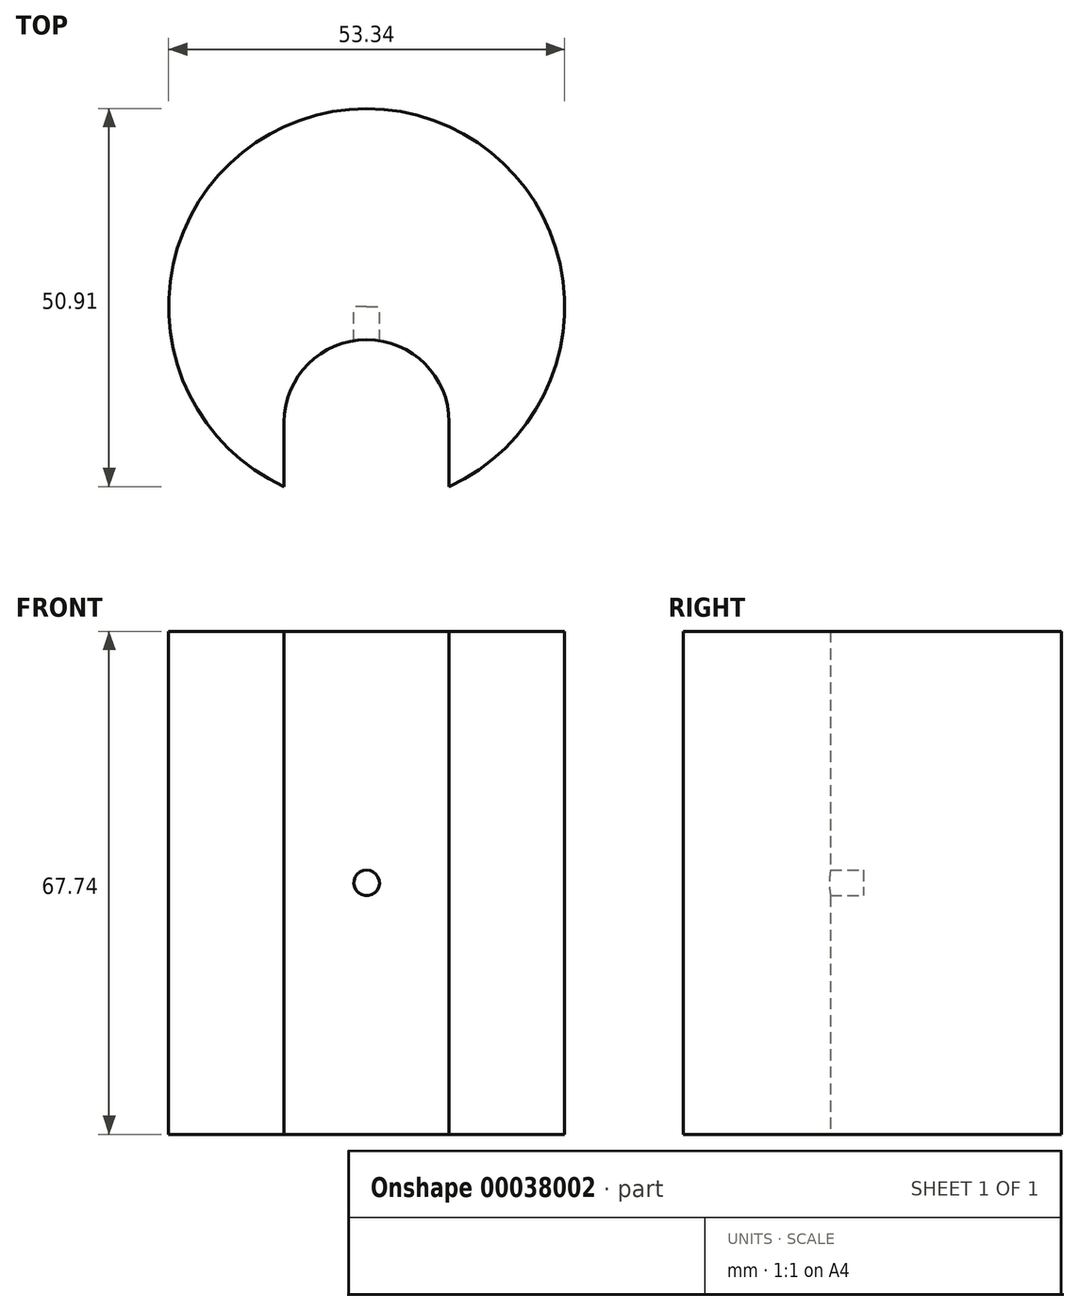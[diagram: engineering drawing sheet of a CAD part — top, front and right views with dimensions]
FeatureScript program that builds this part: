
annotation { "Feature Type Name" : "Feature", "Feature Type Description" : "" }
export const myFeature = defineFeature(function(context is Context, id is Id, definition is map)
    precondition{}
    {
        {
            var Q0;
            Q0=qCreatedBy(makeId("Top.planeOp"),FACE);
            var sketch = newSketch(context, id + "F0", { "sketchPlane" : qUnion([Q0])});
            skCircle(sketch, "E0", {"center": v(0, 0) * mm, "radius": 26.67 * mm});
            skSolve(sketch);
        }
        {
            var Q0;
            Q0 = qSketchRegion(id + "F0", true);
            extrude(context, id + "F1", {"entities" : qUnion([Q0]), "depth" : 67.74 * mm});
        }
        {
            var Q0;
            Q0=makeQuery(id+"F1.opExtrude","CAP_FACE",FACE,{"disambiguationData":[OSD([sQuery(id+"F0.wireOp",EDGE,"E0")])],"isStart":false});
            var sketch = newSketch(context, id + "F2", { "sketchPlane" : qUnion([Q0])});
            skLineSegment(sketch, "E1", {"start": v(0, 0) * mm, "end": v(0, -15.56) * mm, "construction": true});
            skLineSegment(sketch, "E2.rect.bottom", {"start": v(11.11, -26.67) * mm, "end": v(-11.11, -26.67) * mm});
            skLineSegment(sketch, "E2.rect.top", {"start": v(11.11, -4.45) * mm, "end": v(-11.11, -4.45) * mm});
            skLineSegment(sketch, "E2.rect.left", {"start": v(11.11, -26.67) * mm, "end": v(11.11, -4.45) * mm});
            skLineSegment(sketch, "E2.rect.right", {"start": v(-11.11, -26.67) * mm, "end": v(-11.11, -4.45) * mm});
            skPoint(sketch, "E2.rect.middle", {"position": v(0, -15.56) * mm});
            skSolve(sketch);
        }
        {
            var Q0;
            Q0 = qSketchRegion(id + "F2", true);
            var Q1;
            Q1=makeQuery(id+"F1.opExtrude","CAP_FACE",FACE,{"disambiguationData":[OSD([sQuery(id+"F0.wireOp",EDGE,"E0")])],"isStart":true});
            extrude(context, id + "F3", {"entities" : qUnion([Q0]), "operationType" : NewBodyOperationType.REMOVE, "endBound" : BoundingType.UP_TO_SURFACE, "oppositeDirection" : true, "endBoundEntityFace" : qUnion([Q1]), "depth" : 25.4 * mm});
        }
        {
            var Q0;
            Q0=makeQuery(id+"F3.boolean.opBoolean","COPY",EDGE,{"derivedFrom":makeQuery(id+"F3.opExtrude","SWEPT_EDGE",EDGE,{"disambiguationData":[OSD([sQuery(id+"F2.wireOp",EDGE,"E2.rect.top"),sQuery(id+"F2.wireOp",EDGE,"E2.rect.left")])]})});
            var Q1;
            Q1=makeQuery(id+"F3.boolean.opBoolean","COPY",EDGE,{"derivedFrom":makeQuery(id+"F3.opExtrude","SWEPT_EDGE",EDGE,{"disambiguationData":[OSD([sQuery(id+"F2.wireOp",EDGE,"E2.rect.top"),sQuery(id+"F2.wireOp",EDGE,"E2.rect.right")])]})});
            fillet(context, id + "F4", {"entities" : qUnion([Q0, Q1]), "radius" : 11.1 * mm, "tangentPropagation" : true, "allowEdgeOverflow" : false});
        }
        {
            var Q0;
            Q0=qCreatedBy(makeId("Front.planeOp"),FACE);
            var sketch = newSketch(context, id + "F5", { "sketchPlane" : qUnion([Q0])});
            skCircle(sketch, "E3", {"center": v(0, 33.87) * mm, "radius": 1.73 * mm});
            skLineSegment(sketch, "E4", {"start": v(0, 67.74) * mm, "end": v(0, 0) * mm, "construction": true});
            skSolve(sketch);
        }
        {
            var Q0;
            Q0 = qSketchRegion(id + "F5", true);
            var Q1;
            Q1=makeQuery(id+"F4.opFillet","BLEND_FACE",FACE,{"disambiguationData":[OSD([sQuery(id+"F2.wireOp",EDGE,"E2.rect.top"),sQuery(id+"F2.wireOp",EDGE,"E2.rect.right")])]});
            extrude(context, id + "F6", {"entities" : qUnion([Q0]), "operationType" : NewBodyOperationType.REMOVE, "endBound" : BoundingType.UP_TO_SURFACE, "endBoundEntityFace" : qUnion([Q1]), "depth" : 25.4 * mm});
        }
    });
